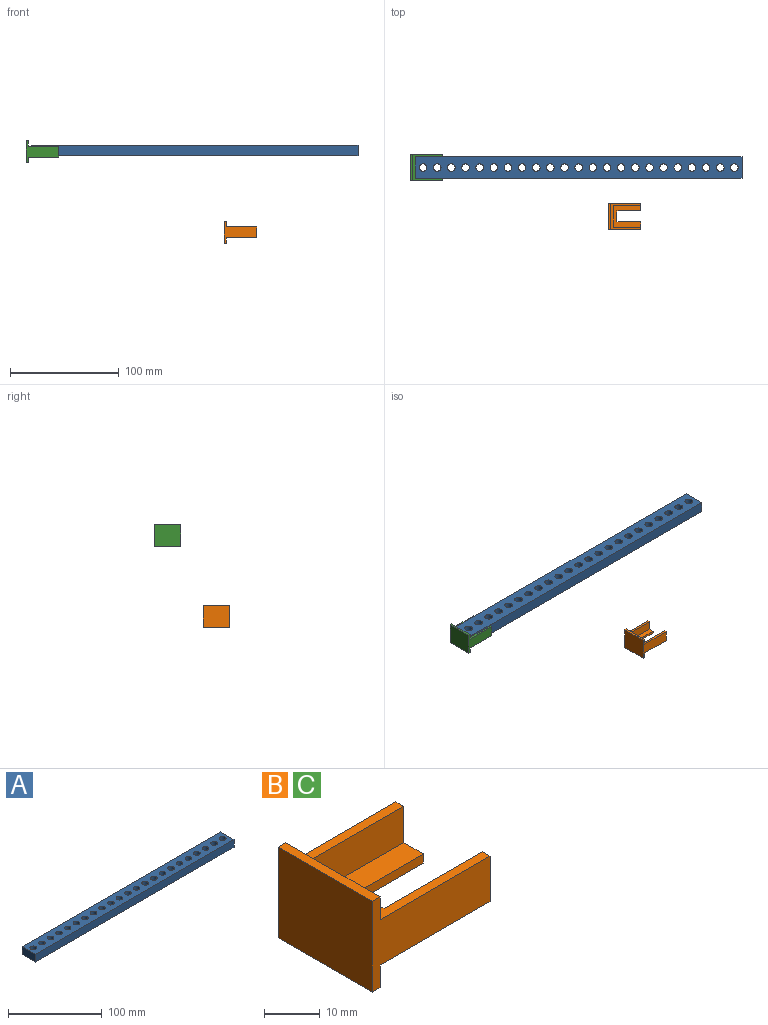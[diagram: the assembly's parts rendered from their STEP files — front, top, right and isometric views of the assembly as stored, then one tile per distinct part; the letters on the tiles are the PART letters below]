
ASSEMBLY  parts=3 mates=1
PART A: 29 faces, bbox 300x20x10 mm
  f0: plane 20x10mm, normal (1,0,0), area 200mm2, adj f1,f26,f27,f28
  f1: plane 300x10mm, normal (0,1,0), area 3000mm2, adj f0,f2,f27,f28
  f2: plane 20x10mm, normal (-1,0,0), area 200mm2, adj f1,f26,f27,f28
  f3: cylinder r=3.5mm len=10mm, axis (0,0,-1), area 219.9mm2, adj f27,f28
  f4: cylinder r=3.5mm len=10mm, axis (0,0,-1), area 219.9mm2, adj f27,f28
  f5: cylinder r=3.5mm len=10mm, axis (0,0,-1), area 219.9mm2, adj f27,f28
  f6: cylinder r=3.5mm len=10mm, axis (0,0,-1), area 219.9mm2, adj f27,f28
  f7: cylinder r=3.5mm len=10mm, axis (0,0,-1), area 219.9mm2, adj f27,f28
  f8: cylinder r=3.5mm len=10mm, axis (0,0,-1), area 219.9mm2, adj f27,f28
  f9: cylinder r=3.5mm len=10mm, axis (0,0,-1), area 219.9mm2, adj f27,f28
  f10: cylinder r=3.5mm len=10mm, axis (0,0,-1), area 219.9mm2, adj f27,f28
  f11: cylinder r=3.5mm len=10mm, axis (0,0,-1), area 219.9mm2, adj f27,f28
  f12: cylinder r=3.5mm len=10mm, axis (0,0,-1), area 219.9mm2, adj f27,f28
  f13: cylinder r=3.5mm len=10mm, axis (0,0,-1), area 219.9mm2, adj f27,f28
  f14: cylinder r=3.5mm len=10mm, axis (0,0,-1), area 219.9mm2, adj f27,f28
  f15: cylinder r=3.5mm len=10mm, axis (0,0,-1), area 219.9mm2, adj f27,f28
  f16: cylinder r=3.5mm len=10mm, axis (0,0,-1), area 219.9mm2, adj f27,f28
  f17: cylinder r=3.5mm len=10mm, axis (0,0,-1), area 219.9mm2, adj f27,f28
  f18: cylinder r=3.5mm len=10mm, axis (0,0,-1), area 219.9mm2, adj f27,f28
  f19: cylinder r=3.5mm len=10mm, axis (0,0,-1), area 219.9mm2, adj f27,f28
  f20: cylinder r=3.5mm len=10mm, axis (0,0,-1), area 219.9mm2, adj f27,f28
  f21: cylinder r=3.5mm len=10mm, axis (0,0,-1), area 219.9mm2, adj f27,f28
  f22: cylinder r=3.5mm len=10mm, axis (0,0,-1), area 219.9mm2, adj f27,f28
  f23: cylinder r=3.5mm len=10mm, axis (0,0,-1), area 219.9mm2, adj f27,f28
  f24: cylinder r=3.5mm len=10mm, axis (0,0,-1), area 219.9mm2, adj f27,f28
  f25: cylinder r=3.5mm len=10mm, axis (0,0,-1), area 219.9mm2, adj f27,f28
  f26: plane 300x10mm, normal (0,-1,0), area 3000mm2, adj f0,f2,f27,f28
  f27: plane 300x20mm, normal (0,0,1), area 5114.9mm2, adj f0,f1,f2,f3,f4,f5,f6,f7
  f28: plane 300x20mm, normal (0,0,-1), area 5114.9mm2, adj f0,f1,f2,f3,f4,f5,f6,f7
PART B: 18 faces, bbox 30x24x20 mm
  f0: plane 22x2mm, normal (0,-1,0), area 44mm2, adj f1,f4,f5,f6
  f1: plane 10x7mm, normal (1,0,0), area 30mm2, adj f0,f5,f6,f7,f10,f12
  f2: plane 10x7mm, normal (1,0,0), area 30mm2, adj f3,f5,f6,f9,f11,f12
  f3: plane 22x2mm, normal (0,1,0), area 44mm2, adj f2,f4,f5,f6
  f4: plane 10x2mm, normal (1,0,0), area 20mm2, adj f0,f3,f5,f6
  f5: plane 25x20mm, normal (0,0,1), area 280mm2, adj f0,f1,f2,f3,f4,f7,f8,f9
  f6: plane 28x24mm, normal (0,0,-1), area 452mm2, adj f0,f1,f2,f3,f4,f10,f11,f13
  f7: plane 25x8mm, normal (0,-1,0), area 200mm2, adj f1,f5,f8,f12
  f8: plane 20x8mm, normal (1,0,0), area 160mm2, adj f5,f7,f9,f12
  f9: plane 25x8mm, normal (0,1,0), area 200mm2, adj f2,f5,f8,f12
  f10: plane 30x20mm, normal (0,1,0), area 320mm2, adj f1,f6,f12,f13,f14,f15,f16,f17
  f11: plane 30x20mm, normal (0,-1,0), area 320mm2, adj f2,f6,f12,f13,f14,f15,f16,f17
  f12: plane 28x24mm, normal (0,0,1), area 172mm2, adj f1,f2,f7,f8,f9,f10,f11,f16
  f13: plane 24x5mm, normal (1,0,0), area 120mm2, adj f6,f10,f11,f15
  f14: plane 24x20mm, normal (-1,0,0), area 480mm2, adj f10,f11,f15,f17
  f15: plane 24x2mm, normal (0,0,-1), area 48mm2, adj f10,f11,f13,f14
  f16: plane 24x5mm, normal (1,0,0), area 120mm2, adj f10,f11,f12,f17
  f17: plane 24x2mm, normal (0,0,1), area 48mm2, adj f10,f11,f14,f16
PART C: same geometry as B
PLACE A at identity
PLACE B t=(42.13,-44.71,-75.28)mm
PLACE C t=(-140,0,-1)mm
MATE planar C.f8 <-> A.f2  axis (1,0,0) through (-150,0,5)mm
